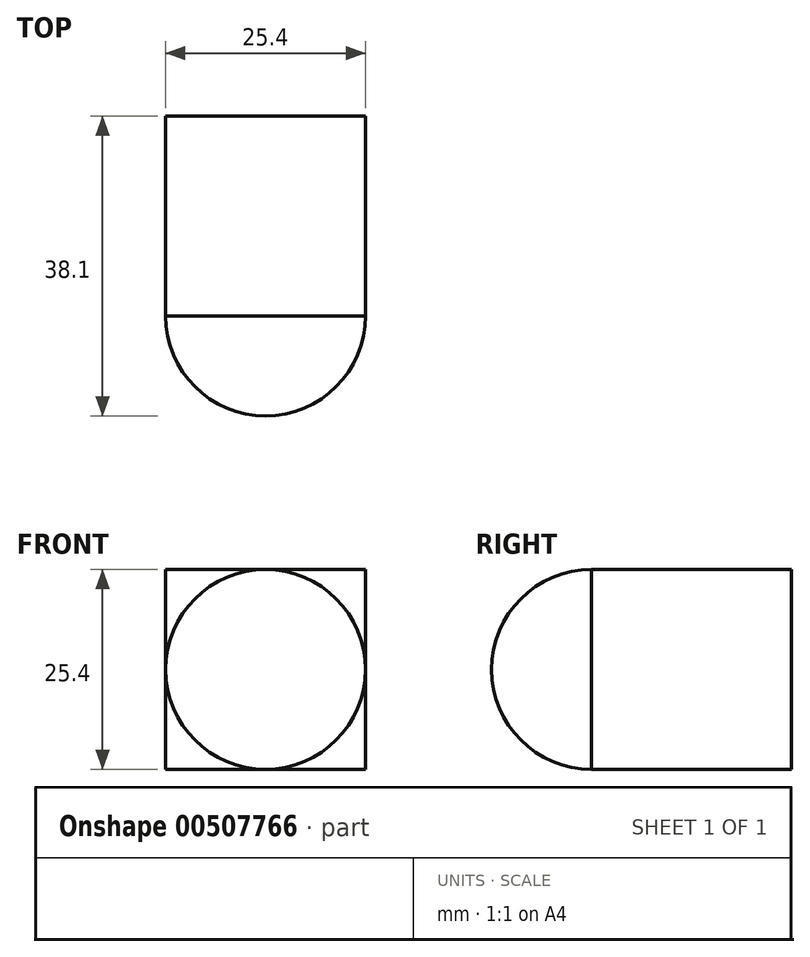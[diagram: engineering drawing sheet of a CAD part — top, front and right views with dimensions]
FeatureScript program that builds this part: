
annotation { "Feature Type Name" : "Feature", "Feature Type Description" : "" }
export const myFeature = defineFeature(function(context is Context, id is Id, definition is map)
    precondition{}
    {
        {
            var Q0;
            Q0=qCreatedBy(makeId("Front.planeOp"),FACE);
            var sketch = newSketch(context, id + "F0", { "sketchPlane" : qUnion([Q0])});
            skLineSegment(sketch, "E0.bottom", {"start": v(-12.7, 12.7) * mm, "end": v(12.7, 12.7) * mm});
            skLineSegment(sketch, "E0.top", {"start": v(-12.7, -12.7) * mm, "end": v(12.7, -12.7) * mm});
            skLineSegment(sketch, "E0.left", {"start": v(-12.7, 12.7) * mm, "end": v(-12.7, -12.7) * mm});
            skLineSegment(sketch, "E0.right", {"start": v(12.7, 12.7) * mm, "end": v(12.7, -12.7) * mm});
            skLineSegment(sketch, "E1", {"start": v(0, 12.7) * mm, "end": v(0, -12.7) * mm, "construction": true});
            skSolve(sketch);
        }
        {
            var Q0;
            Q0 = qSketchRegion(id + "F0", true);
            extrude(context, id + "F1", {"entities" : qUnion([Q0]), "depth" : 25.4 * mm});
        }
        {
            var Q0;
            Q0=makeQuery(id+"F1.opExtrude","CAP_FACE",FACE,{"disambiguationData":[OSD([sQuery(id+"F0.wireOp",EDGE,"E0.bottom"),sQuery(id+"F0.wireOp",EDGE,"E0.top"),sQuery(id+"F0.wireOp",EDGE,"E0.left"),sQuery(id+"F0.wireOp",EDGE,"E0.right")])],"isStart":false});
            var sketch = newSketch(context, id + "F2", { "sketchPlane" : qUnion([Q0])});
            skLineSegment(sketch, "E2", {"start": v(0, 12.7) * mm, "end": v(0, -12.7) * mm});
            skArc(sketch, "E3", {"start": v(0, 12.7) * mm, "mid": v(-12.7, 0) * mm, "end": v(0, -12.7) * mm});
            skSolve(sketch);
        }
        {
            var Q0;
            {var subQ0=sQuery(id+"F2.wireOp",EDGE,"E2");Q0=makeQuery(id+"F2.imprint","IMPRINT",FACE,{"disambiguationData":[TD([[makeQuery(id+"F2.imprint","IMPRINT",EDGE,{"derivedFrom":subQ0}),-1.0]])]});}
            var Q1;
            Q1=sQuery(id+"F2.wireOp",EDGE,"E2");
            revolve(context, id + "F3", {"operationType" : NewBodyOperationType.ADD, "entities" : qUnion([Q0]), "axis" : qUnion([Q1]), "revolveType" : RevolveType.FULL});
        }
    });
